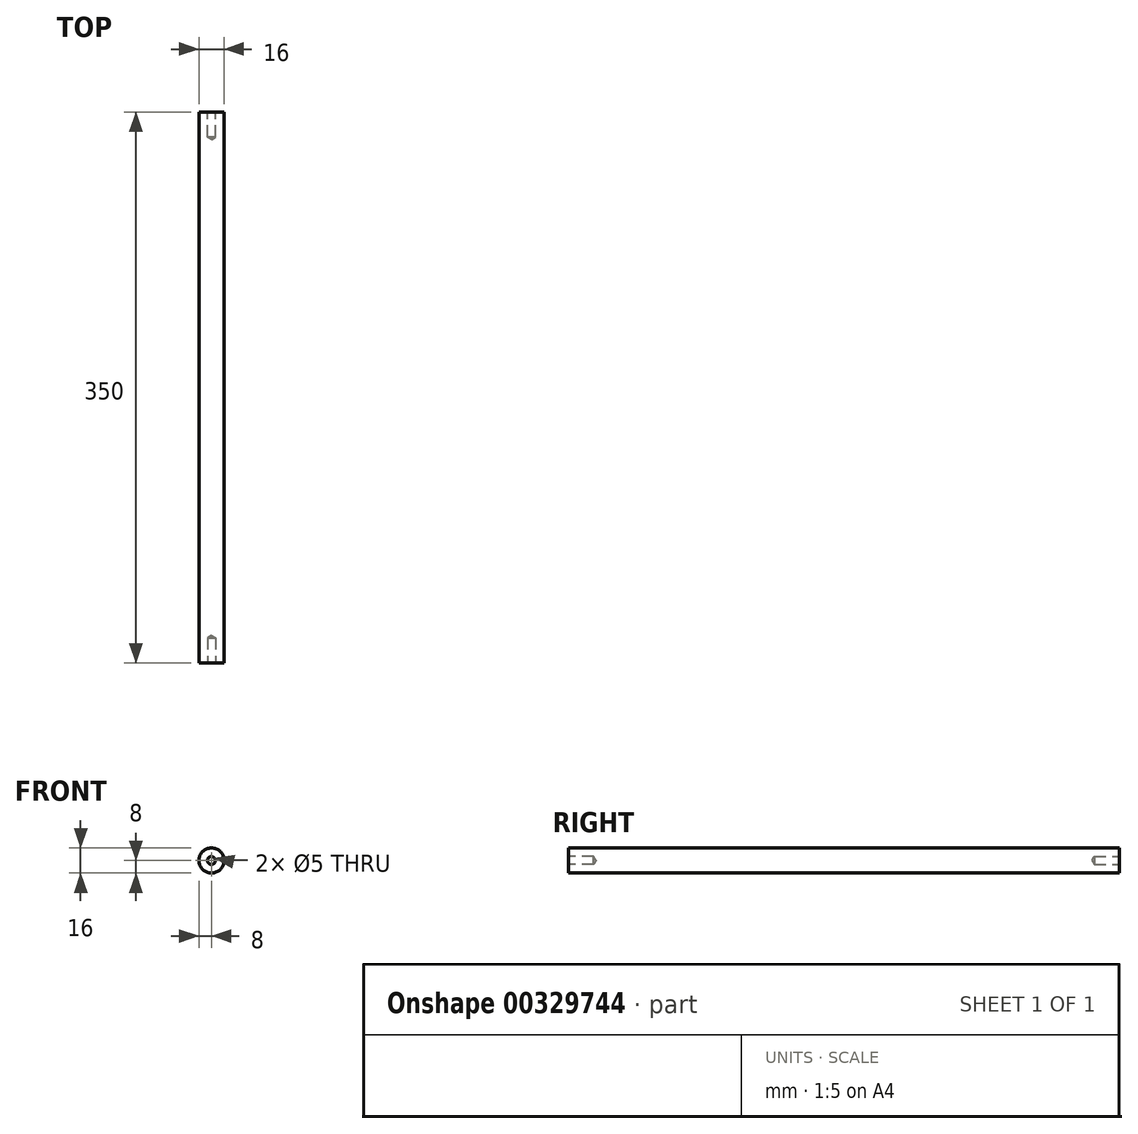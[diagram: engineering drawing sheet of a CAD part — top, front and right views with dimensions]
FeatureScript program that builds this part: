
annotation { "Feature Type Name" : "Feature", "Feature Type Description" : "" }
export const myFeature = defineFeature(function(context is Context, id is Id, definition is map)
    precondition{}
    {
        {
            var Q0;
            Q0=qCreatedBy(makeId("Front.planeOp"),FACE);
            var sketch = newSketch(context, id + "F0", { "sketchPlane" : qUnion([Q0])});
            skCircle(sketch, "E0", {"center": v(0, 0) * mm, "radius": 8 * mm});
            skLineSegment(sketch, "E1", {"start": v(0, 39.86) * mm, "end": v(0, -22.1) * mm, "construction": true});
            skLineSegment(sketch, "E2", {"start": v(0, -22.1) * mm, "end": v(44.9, 0) * mm, "construction": true});
            skLineSegment(sketch, "E3", {"start": v(44.9, 0) * mm, "end": v(-42.5, 0) * mm, "construction": true});
            skSolve(sketch);
        }
        {
            var Q0;
            Q0=qSketchRegion(id+"F0",true);
            extrude(context, id + "F1", {"entities" : qUnion([Q0]), "depth" : 350 * mm});
        }
        {
            var Q0;
            Q0=makeQuery(id+"F1.opExtrude","CAP_FACE",FACE,{"disambiguationData":[OSD([sQuery(id+"F0.wireOp",EDGE,"E0")])],"isStart":true});
            var sketch = newSketch(context, id + "F2", { "sketchPlane" : qUnion([Q0])});
            skPoint(sketch, "E4", {"position": v(0, 0) * mm});
            skSolve(sketch);
        }
        {
            var Q0;
            Q0=makeQuery(id+"F2.imprint","IMPRINT",FACE,{"disambiguationData":[TD([[makeQuery(id+"F2.imprint","IMPRINT",EDGE,{"derivedFrom":makeQuery(id+"F1.opExtrude","CAP_EDGE",EDGE,{"disambiguationData":[OSD([sQuery(id+"F0.wireOp",EDGE,"E0")])],"isStart":true})}),-1.0]])]});
            var sketch = newSketch(context, id + "F3", { "sketchPlane" : qUnion([Q0])});
            skPoint(sketch, "E5", {"position": v(0, 0) * mm});
            skSolve(sketch);
        }
        {
            var Q0;
            Q0=sQuery(id+"F3.wireOp",VERTEX,"E5");
            var Q1;
            Q1=makeQuery(id+"F1.opExtrude","SWEPT_BODY",BODY,{"disambiguationData":[OSD([sQuery(id+"F0.wireOp",EDGE,"E0")])]});
            hole(context, id + "F4", {"style" : HoleStyle.SIMPLE, "endStyle" : HoleEndStyle.BLIND, "standardTappedOrClearance" : lookupTablePath({ "standard" : "ISO", "engagement" : "75%", "pitch" : "1 mm", "size" : "M6", "type" : "Tapped" }), "standardBlindInLast" : lookupTablePath({ "standard" : "ISO", "engagement" : "75%", "pitch" : "1 mm", "size" : "M6", "type" : "Tapped" }), "holeDiameter" : 5 * mm, "showTappedDepth" : true, "holeDepth" : 16 * mm, "tappedDepth" : 15 * mm, "tapClearance" : 1, "locations" : qUnion([Q0]), "scope" : qUnion([Q1]), "majorDiameter" : 6 * mm});
        }
        {
            var Q0;
            Q0=makeQuery(id+"F1.opExtrude","CAP_FACE",FACE,{"disambiguationData":[OSD([sQuery(id+"F0.wireOp",EDGE,"E0")])],"isStart":false});
            var sketch = newSketch(context, id + "F5", { "sketchPlane" : qUnion([Q0])});
            skPoint(sketch, "E6", {"position": v(0, 0) * mm});
            skSolve(sketch);
        }
        {
            var Q0;
            Q0=sQuery(id+"F5.wireOp",VERTEX,"E6");
            var Q1;
            Q1=makeQuery(id+"F1.opExtrude","SWEPT_BODY",BODY,{"disambiguationData":[OSD([sQuery(id+"F0.wireOp",EDGE,"E0")])]});
            hole(context, id + "F6", {"style" : HoleStyle.SIMPLE, "endStyle" : HoleEndStyle.BLIND, "standardTappedOrClearance" : lookupTablePath({ "standard" : "ISO", "engagement" : "75%", "pitch" : "1 mm", "size" : "M6", "type" : "Tapped" }), "standardBlindInLast" : lookupTablePath({ "standard" : "ISO", "engagement" : "75%", "pitch" : "1 mm", "size" : "M6", "type" : "Tapped" }), "holeDiameter" : 5 * mm, "showTappedDepth" : true, "holeDepth" : 16 * mm, "tappedDepth" : 15 * mm, "tapClearance" : 1, "locations" : qUnion([Q0]), "scope" : qUnion([Q1]), "majorDiameter" : 6 * mm});
        }
    });
